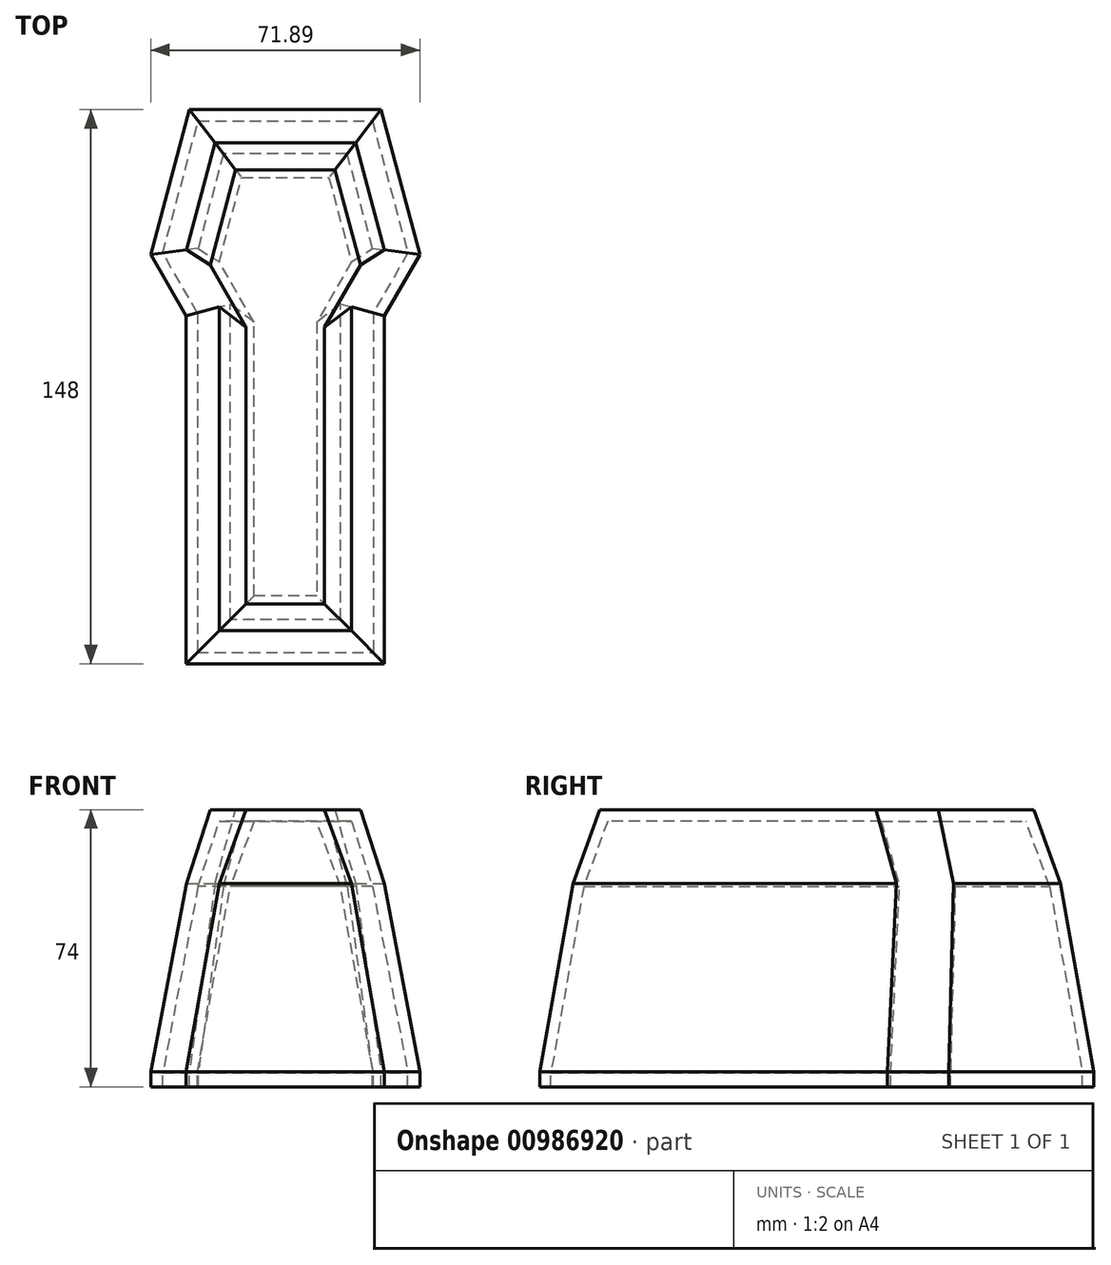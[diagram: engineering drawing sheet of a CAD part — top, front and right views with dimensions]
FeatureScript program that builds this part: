
annotation { "Feature Type Name" : "Feature", "Feature Type Description" : "" }
export const myFeature = defineFeature(function(context is Context, id is Id, definition is map)
    precondition{}
    {
        {
            var Q0;
            Q0=qCreatedBy(makeId("Top.planeOp"),FACE);
            var sketch = newSketch(context, id + "F0", { "sketchPlane" : qUnion([Q0])});
            skPoint(sketch, "E0.middle", {"position": v(-76.7, -52.8) * mm});
            skLineSegment(sketch, "E1.0", {"start": v(-103.2, -8.88) * mm, "end": v(-112.65, 7.48) * mm});
            skLineSegment(sketch, "E1.1", {"start": v(-112.65, 7.48) * mm, "end": v(-102.27, 46.2) * mm});
            skLineSegment(sketch, "E1.2", {"start": v(-103.2, -8.88) * mm, "end": v(-103.2, -101.8) * mm});
            skLineSegment(sketch, "E1.3", {"start": v(-102.27, 46.2) * mm, "end": v(-51.13, 46.2) * mm});
            skLineSegment(sketch, "E1.4", {"start": v(-103.2, -101.8) * mm, "end": v(-50.2, -101.8) * mm});
            skLineSegment(sketch, "E1.5", {"start": v(-50.2, -8.88) * mm, "end": v(-50.2, -101.8) * mm});
            skLineSegment(sketch, "E1.6", {"start": v(-40.76, 7.48) * mm, "end": v(-50.2, -8.88) * mm});
            skLineSegment(sketch, "E1.7", {"start": v(-51.13, 46.2) * mm, "end": v(-40.76, 7.48) * mm});
            skSolve(sketch);
        }
        {
            var Q0;
            Q0 = qSketchRegion(id + "F0", true);
            extrude(context, id + "F1", {"entities" : qUnion([Q0]), "depth" : 70 * mm, "offsetDistance" : 25 * mm, "hasDraft" : true, "draftAngle" : 10 * degree, "draftPullDirection" : true});
        }
        {
            var Q0;
            Q0 = qSketchRegion(id + "F0", true);
            extrude(context, id + "F2", {"entities" : qUnion([Q0]), "operationType" : NewBodyOperationType.ADD, "oppositeDirection" : true, "depth" : 4 * mm, "offsetDistance" : 25 * mm});
        }
        {
            var Q0;
            Q0=makeQuery(id+"F1.opExtrude","CAP_EDGE",EDGE,{"disambiguationData":[OSD([sQuery(id+"F0.wireOp",EDGE,"E1.3")])],"isStart":false});
            var Q1;
            Q1=makeQuery(id+"F1.opExtrude","CAP_EDGE",EDGE,{"disambiguationData":[OSD([sQuery(id+"F0.wireOp",EDGE,"E1.1")])],"isStart":false});
            var Q2;
            Q2=makeQuery(id+"F1.opExtrude","CAP_EDGE",EDGE,{"disambiguationData":[OSD([sQuery(id+"F0.wireOp",EDGE,"E1.7")])],"isStart":false});
            var Q3;
            Q3=makeQuery(id+"F1.opExtrude","CAP_EDGE",EDGE,{"disambiguationData":[OSD([sQuery(id+"F0.wireOp",EDGE,"E1.5")])],"isStart":false});
            var Q4;
            Q4=makeQuery(id+"F1.opExtrude","CAP_EDGE",EDGE,{"disambiguationData":[OSD([sQuery(id+"F0.wireOp",EDGE,"E1.2")])],"isStart":false});
            var Q5;
            Q5=makeQuery(id+"F1.opExtrude","CAP_EDGE",EDGE,{"disambiguationData":[OSD([sQuery(id+"F0.wireOp",EDGE,"E1.4")])],"isStart":false});
            chamfer(context, id + "F3", {"entities" : qUnion([Q0, Q1, Q2, Q3, Q4, Q5]), "chamferType" : ChamferType.OFFSET_ANGLE, "width" : 20 * mm, "oppositeDirection" : false, "angle" : 10 * degree, "tangentPropagation" : true});
        }
        {
            var Q0;
            Q0=makeQuery(id+"F2.opExtrude","CAP_FACE",FACE,{"disambiguationData":[OSD([sQuery(id+"F0.wireOp",EDGE,"E1.0"),sQuery(id+"F0.wireOp",EDGE,"E1.1"),sQuery(id+"F0.wireOp",EDGE,"E1.2"),sQuery(id+"F0.wireOp",EDGE,"E1.3"),sQuery(id+"F0.wireOp",EDGE,"E1.4"),sQuery(id+"F0.wireOp",EDGE,"E1.5"),sQuery(id+"F0.wireOp",EDGE,"E1.6"),sQuery(id+"F0.wireOp",EDGE,"E1.7")])],"isStart":false});
            shell(context, id + "F4", {"entities" : qUnion([Q0]), "thickness" : 3 * mm});
        }
    });
